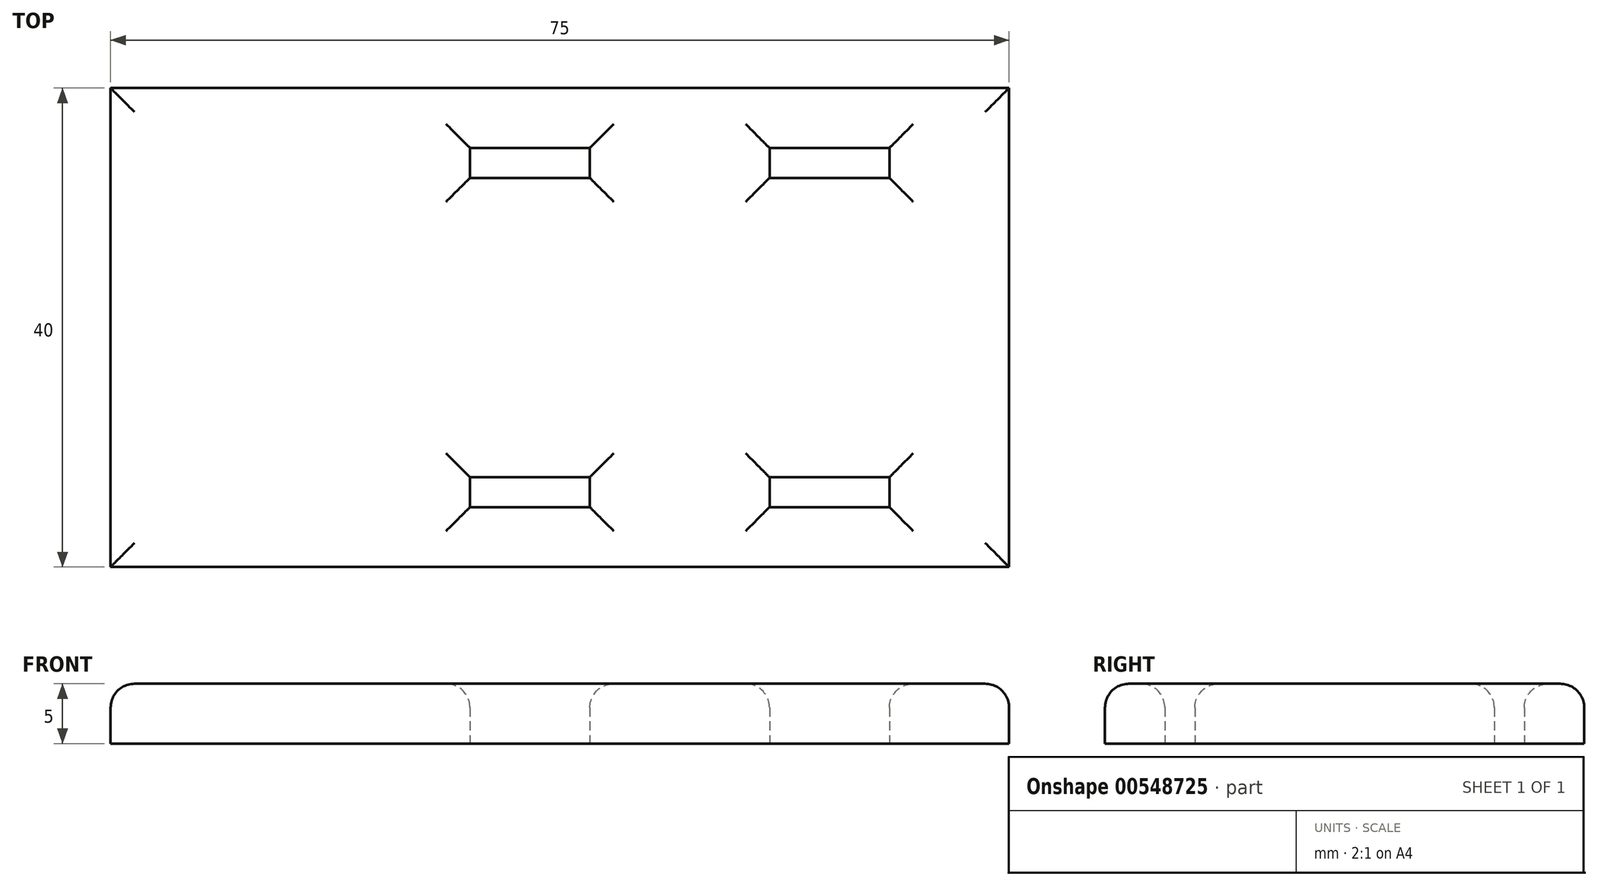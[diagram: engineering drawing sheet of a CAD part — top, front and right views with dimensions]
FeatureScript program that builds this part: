
annotation { "Feature Type Name" : "Feature", "Feature Type Description" : "" }
export const myFeature = defineFeature(function(context is Context, id is Id, definition is map)
    precondition{}
    {
        {
            var Q0;
            Q0=qCreatedBy(makeId("Top.planeOp"),FACE);
            var sketch = newSketch(context, id + "F0", { "sketchPlane" : qUnion([Q0])});
            skLineSegment(sketch, "E0.bottom", {"start": v(-61.17, 0) * mm, "end": v(13.83, 0) * mm});
            skLineSegment(sketch, "E0.top", {"start": v(-61.17, -40) * mm, "end": v(13.83, -40) * mm});
            skLineSegment(sketch, "E0.left", {"start": v(-61.17, 0) * mm, "end": v(-61.17, -40) * mm});
            skLineSegment(sketch, "E0.right", {"start": v(13.83, 0) * mm, "end": v(13.83, -40) * mm});
            skLineSegment(sketch, "E1.bottom", {"start": v(-31.17, -35) * mm, "end": v(-21.17, -35) * mm});
            skLineSegment(sketch, "E1.top", {"start": v(-31.17, -32.5) * mm, "end": v(-21.17, -32.5) * mm});
            skLineSegment(sketch, "E1.left", {"start": v(-31.17, -35) * mm, "end": v(-31.17, -32.5) * mm});
            skLineSegment(sketch, "E1.right", {"start": v(-21.17, -35) * mm, "end": v(-21.17, -32.5) * mm});
            skLineSegment(sketch, "E2.bottom", {"start": v(-6.17, -35) * mm, "end": v(3.83, -35) * mm});
            skLineSegment(sketch, "E2.top", {"start": v(-6.17, -32.5) * mm, "end": v(3.83, -32.5) * mm});
            skLineSegment(sketch, "E2.left", {"start": v(-6.17, -35) * mm, "end": v(-6.17, -32.5) * mm});
            skLineSegment(sketch, "E2.right", {"start": v(3.83, -35) * mm, "end": v(3.83, -32.5) * mm});
            skLineSegment(sketch, "E3.bottom", {"start": v(-6.17, -7.5) * mm, "end": v(3.83, -7.5) * mm});
            skLineSegment(sketch, "E3.top", {"start": v(-6.17, -5) * mm, "end": v(3.83, -5) * mm});
            skLineSegment(sketch, "E3.left", {"start": v(-6.17, -7.5) * mm, "end": v(-6.17, -5) * mm});
            skLineSegment(sketch, "E3.right", {"start": v(3.83, -7.5) * mm, "end": v(3.83, -5) * mm});
            skLineSegment(sketch, "E4.bottom", {"start": v(-31.17, -7.5) * mm, "end": v(-21.17, -7.5) * mm});
            skLineSegment(sketch, "E4.top", {"start": v(-31.17, -5) * mm, "end": v(-21.17, -5) * mm});
            skLineSegment(sketch, "E4.left", {"start": v(-31.17, -7.5) * mm, "end": v(-31.17, -5) * mm});
            skLineSegment(sketch, "E4.right", {"start": v(-21.17, -7.5) * mm, "end": v(-21.17, -5) * mm});
            skLineSegment(sketch, "E5", {"start": v(3.83, -7.5) * mm, "end": v(13.83, -7.5) * mm});
            skLineSegment(sketch, "E6", {"start": v(-21.17, -7.5) * mm, "end": v(-6.17, -7.5) * mm});
            skLineSegment(sketch, "E7", {"start": v(-21.17, -32.5) * mm, "end": v(-6.17, -32.5) * mm});
            skLineSegment(sketch, "E8", {"start": v(3.83, -32.5) * mm, "end": v(13.83, -32.5) * mm});
            skLineSegment(sketch, "E9", {"start": v(13.83, -32.5) * mm, "end": v(13.83, -40) * mm});
            skSolve(sketch);
        }
        {
            var Q0;
            Q0=makeQuery(id+"F0.imprint","IMPRINT",FACE,{"disambiguationData":[TD([[makeQuery(id+"F0.imprint","IMPRINT",EDGE,{"derivedFrom":sQuery(id+"F0.wireOp",EDGE,"E0.bottom")}),-1.0]])]});
            extrude(context, id + "F1", {"entities" : qUnion([Q0]), "depth" : 5 * mm, "offsetDistance" : 25.4 * mm});
        }
        {
            var Q0;
            Q0=makeQuery(id+"F1.opExtrude","CAP_EDGE",EDGE,{"disambiguationData":[OSD([sQuery(id+"F0.wireOp",EDGE,"E3.top")])],"isStart":false});
            var Q1;
            Q1=makeQuery(id+"F1.opExtrude","CAP_EDGE",EDGE,{"disambiguationData":[OSD([sQuery(id+"F0.wireOp",EDGE,"E3.right")])],"isStart":false});
            var Q2;
            Q2=makeQuery(id+"F1.opExtrude","CAP_EDGE",EDGE,{"disambiguationData":[OSD([sQuery(id+"F0.wireOp",EDGE,"E3.bottom")])],"isStart":false});
            var Q3;
            Q3=makeQuery(id+"F1.opExtrude","CAP_EDGE",EDGE,{"disambiguationData":[OSD([sQuery(id+"F0.wireOp",EDGE,"E3.left")])],"isStart":false});
            var Q4;
            Q4=makeQuery(id+"F1.opExtrude","CAP_EDGE",EDGE,{"disambiguationData":[OSD([sQuery(id+"F0.wireOp",EDGE,"E4.right")])],"isStart":false});
            var Q5;
            Q5=makeQuery(id+"F1.opExtrude","CAP_EDGE",EDGE,{"disambiguationData":[OSD([sQuery(id+"F0.wireOp",EDGE,"E4.top")])],"isStart":false});
            var Q6;
            Q6=makeQuery(id+"F1.opExtrude","CAP_EDGE",EDGE,{"disambiguationData":[OSD([sQuery(id+"F0.wireOp",EDGE,"E4.bottom")])],"isStart":false});
            var Q7;
            Q7=makeQuery(id+"F1.opExtrude","CAP_FACE",FACE,{"disambiguationData":[OSD([sQuery(id+"F0.wireOp",EDGE,"E0.bottom"),sQuery(id+"F0.wireOp",EDGE,"E0.top"),sQuery(id+"F0.wireOp",EDGE,"E0.left"),sQuery(id+"F0.wireOp",EDGE,"E0.right"),sQuery(id+"F0.wireOp",EDGE,"E1.bottom"),sQuery(id+"F0.wireOp",EDGE,"E1.top"),sQuery(id+"F0.wireOp",EDGE,"E1.left"),sQuery(id+"F0.wireOp",EDGE,"E1.right"),sQuery(id+"F0.wireOp",EDGE,"E2.bottom"),sQuery(id+"F0.wireOp",EDGE,"E2.top"),sQuery(id+"F0.wireOp",EDGE,"E2.left"),sQuery(id+"F0.wireOp",EDGE,"E2.right"),sQuery(id+"F0.wireOp",EDGE,"E3.bottom"),sQuery(id+"F0.wireOp",EDGE,"E3.top"),sQuery(id+"F0.wireOp",EDGE,"E3.left"),sQuery(id+"F0.wireOp",EDGE,"E3.right"),sQuery(id+"F0.wireOp",EDGE,"E4.bottom"),sQuery(id+"F0.wireOp",EDGE,"E4.top"),sQuery(id+"F0.wireOp",EDGE,"E4.left"),sQuery(id+"F0.wireOp",EDGE,"E4.right"),sQuery(id+"F0.wireOp",EDGE,"E9")])],"isStart":false});
            fillet(context, id + "F2", {"entities" : qUnion([Q0, Q1, Q2, Q3, Q4, Q5, Q6, Q7]), "radius" : 2 * mm, "tangentPropagation" : true, "allowEdgeOverflow" : false});
        }
    });
